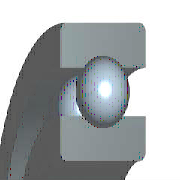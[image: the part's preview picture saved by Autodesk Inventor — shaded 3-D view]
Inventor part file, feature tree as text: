
AUTODESK INVENTOR PART (.ipt)
format: ipt  version: 2015 SP2 (Build 190223200, 223)  size: 346,112 bytes
history: native  units: mm (DEFAULTED — no unit token found)
features: sketch x5, other x3, plane x2, pattern_circular x1, fillet x1
ambient origin geometry x8: Origin, YZ Plane, XZ Plane, XY Plane, X Axis, Y Axis, Z Axis, Center Point
bodies: Solid1 (feature_tree)
feature tree (12):
  sketch  "Sketch1"  dims[d2=72.0mm]
  other  "WorkPoint1"
  other  "WorkAxis1"
  plane  "WorkPlane3"
  plane  "WorkPlane4"
  sketch  "Sketch4"  dims[d5=5.0mm]
  other  "WorkPoint2"
  pattern_circular  "PolarArray1"  Count=2  [1 undecoded]
  fillet  "Fillet1"  Radius=4.0mm
  sketch  "Sketch2"  dims[d3=13.0mm]
  sketch  "Sketch3"  dims[d4=19.0mm]
  sketch  "Sketch5"  dims[d6=360.0deg d7=0.0mm d8=15.6mm d9=2.7mm d10=360.0deg d11=-5.0mm d12=0.0mm d13=0.0mm d14=15.6001mm d15=2.7001mm d16=360.0deg d17=51.222222mm d19=360.0deg d20=0.2mm d21=3.44mm d22=4.25mm d23=5.06mm d26=0.0mm d27=0.0mm d28=0.0mm d29=0.0mm d30=0.0mm]
note: 1 required parameter value undecoded (feature->parameter linkage not recoverable at this tier; creation-order binding heuristic only, values carry confidence <= 0.55)
